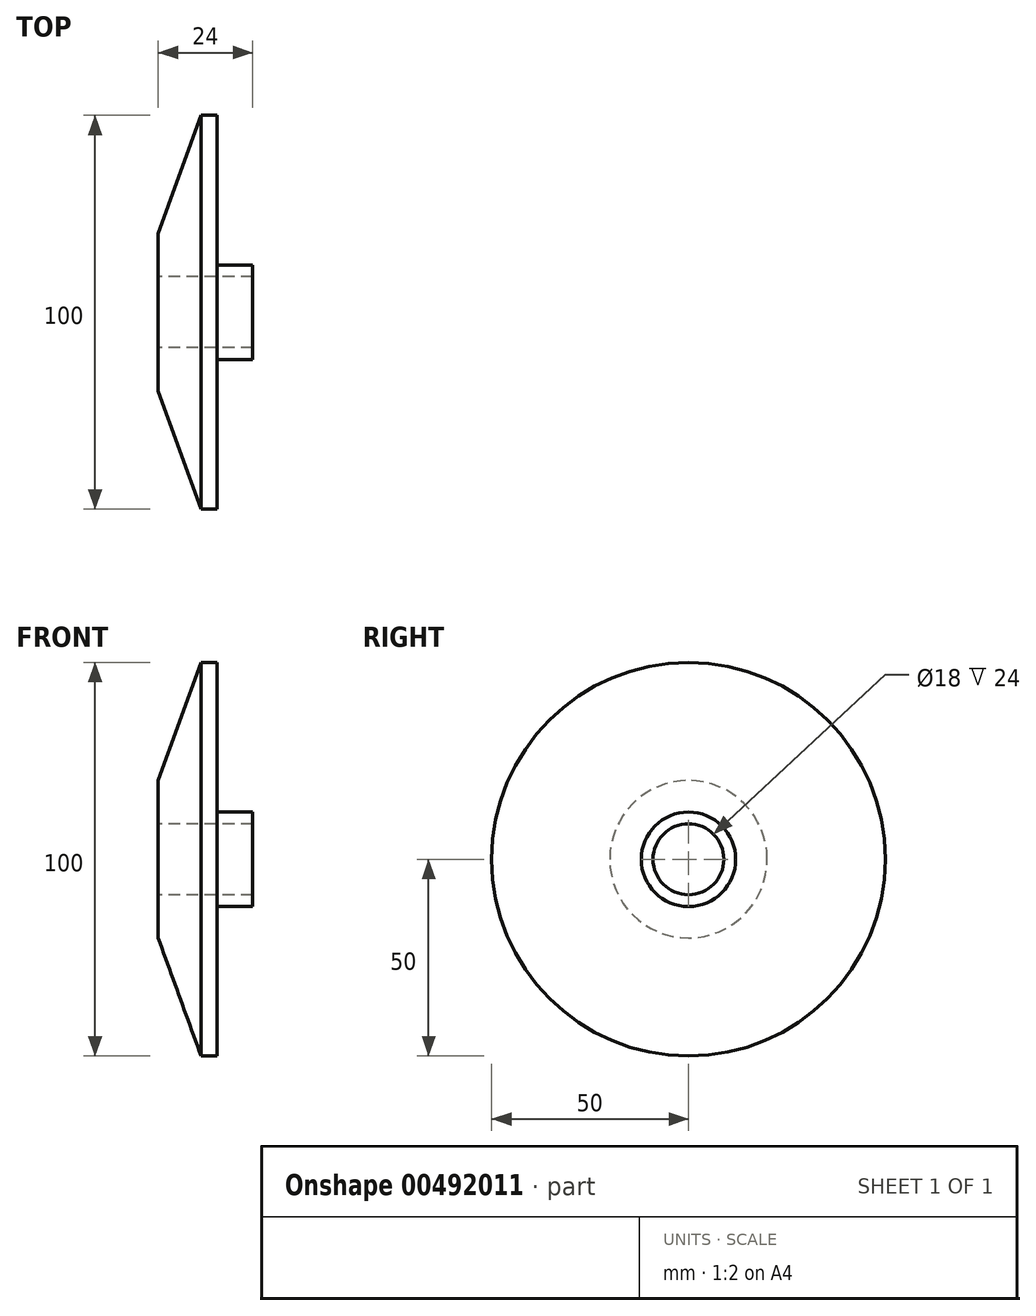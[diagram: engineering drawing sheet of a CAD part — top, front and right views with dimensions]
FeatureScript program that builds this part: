
annotation { "Feature Type Name" : "Feature", "Feature Type Description" : "" }
export const myFeature = defineFeature(function(context is Context, id is Id, definition is map)
    precondition{}
    {
        {
            var Q0;
            Q0=qCreatedBy(makeId("Front.planeOp"),FACE);
            var sketch = newSketch(context, id + "F0", { "sketchPlane" : qUnion([Q0])});
            skLineSegment(sketch, "E0", {"start": v(0, 20) * mm, "end": v(10.92, 50) * mm});
            skLineSegment(sketch, "E1", {"start": v(10.92, 50) * mm, "end": v(15, 50) * mm});
            skLineSegment(sketch, "E2", {"start": v(15, 50) * mm, "end": v(15, 12) * mm});
            skLineSegment(sketch, "E3", {"start": v(15, 12) * mm, "end": v(24, 12) * mm});
            skLineSegment(sketch, "E4", {"start": v(24, 12) * mm, "end": v(24, 0) * mm});
            skLineSegment(sketch, "E5", {"start": v(24, 0) * mm, "end": v(0, 0) * mm});
            skLineSegment(sketch, "E6", {"start": v(0, 0) * mm, "end": v(0, 20) * mm});
            skSolve(sketch);
        }
        {
            var Q0;
            Q0=makeQuery(id+"F0.imprint","IMPRINT",FACE,{"disambiguationData":[TD([[makeQuery(id+"F0.imprint","IMPRINT",EDGE,{"derivedFrom":sQuery(id+"F0.wireOp",EDGE,"E0")}),-1.0]])]});
            var Q1;
            Q1=sQuery(id+"F0.wireOp",EDGE,"E5");
            revolve(context, id + "F1", {"entities" : qUnion([Q0]), "axis" : qUnion([Q1]), "revolveType" : RevolveType.FULL});
        }
        {
            var Q0;
            Q0=qCreatedBy(makeId("Right.planeOp"),FACE);
            var sketch = newSketch(context, id + "F2", { "sketchPlane" : qUnion([Q0])});
            skPoint(sketch, "E7", {"position": v(0, 0) * mm});
            skSolve(sketch);
        }
        {
            var Q0;
            Q0=sQuery(id+"F2.wireOp",VERTEX,"E7");
            var Q1;
            Q1=makeQuery(id+"F1.opRevolve","SWEPT_BODY",BODY,{"disambiguationData":[OSD([sQuery(id+"F0.wireOp",EDGE,"E0"),sQuery(id+"F0.wireOp",EDGE,"E1"),sQuery(id+"F0.wireOp",EDGE,"E2"),sQuery(id+"F0.wireOp",EDGE,"E3"),sQuery(id+"F0.wireOp",EDGE,"E4"),sQuery(id+"F0.wireOp",EDGE,"E5"),sQuery(id+"F0.wireOp",EDGE,"E6")])]});
            hole(context, id + "F3", {"style" : HoleStyle.SIMPLE, "endStyle" : HoleEndStyle.THROUGH, "oppositeDirection" : true, "holeDiameter" : 18 * mm, "isTappedThrough" : true, "tappedDepth" : 12 * mm, "tapClearance" : 3, "locations" : qUnion([Q0]), "scope" : qUnion([Q1])});
        }
    });
